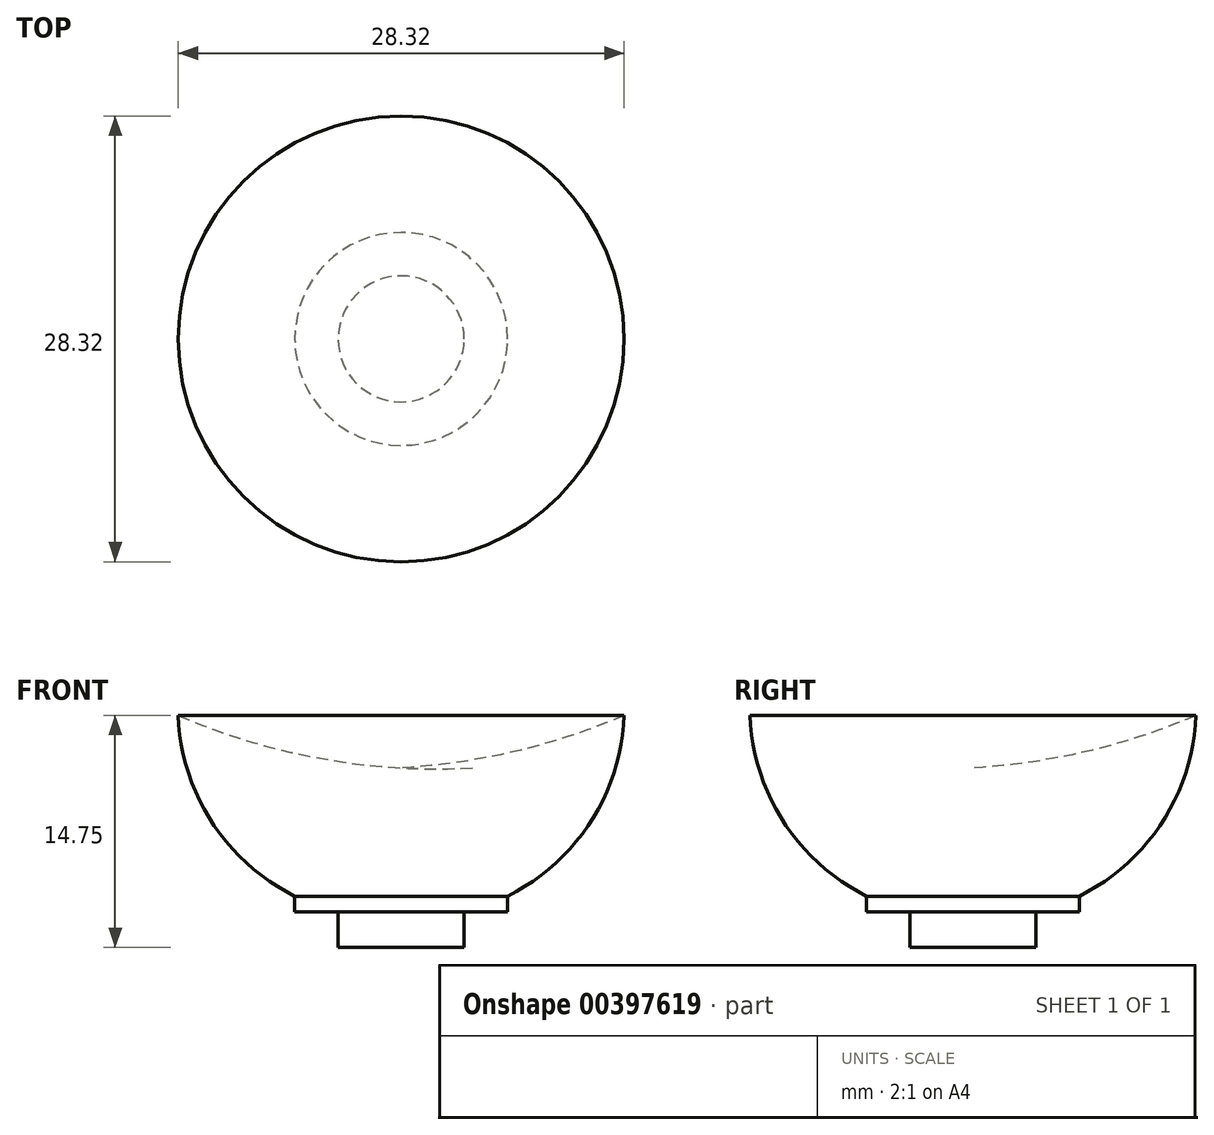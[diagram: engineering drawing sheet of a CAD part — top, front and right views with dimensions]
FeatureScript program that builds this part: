
annotation { "Feature Type Name" : "Feature", "Feature Type Description" : "" }
export const myFeature = defineFeature(function(context is Context, id is Id, definition is map)
    precondition{}
    {
        {
            var Q0;
            Q0=qCreatedBy(makeId("Front.planeOp"),FACE);
            var sketch = newSketch(context, id + "F0", { "sketchPlane" : qUnion([Q0])});
            skLineSegment(sketch, "E0", {"start": v(0, 0) * mm, "end": v(4, 0) * mm});
            skLineSegment(sketch, "E1", {"start": v(4, 0) * mm, "end": v(4, 2.25) * mm});
            skLineSegment(sketch, "E2", {"start": v(4, 2.25) * mm, "end": v(4, 14.75) * mm});
            skArc(sketch, "E3", {"start": v(4, 2.25) * mm, "mid": v(11.17, 6.8) * mm, "end": v(14.16, 14.75) * mm});
            skArc(sketch, "E4", {"start": v(0, 11.41) * mm, "mid": v(7.23, 12.46) * mm, "end": v(14.16, 14.75) * mm});
            skLineSegment(sketch, "E5", {"start": v(0, 11.41) * mm, "end": v(0, 0) * mm});
            skLineSegment(sketch, "E6", {"start": v(4, 2.25) * mm, "end": v(6.76, 2.25) * mm});
            skLineSegment(sketch, "E7", {"start": v(6.76, 2.25) * mm, "end": v(6.76, 3.26) * mm});
            skSolve(sketch);
        }
        {
            var Q0;
            Q0 = qSketchRegion(id + "F0", true);
            var Q1;
            Q1=sQuery(id+"F0.wireOp",EDGE,"E5");
            revolve(context, id + "F1", {"entities" : qUnion([Q0]), "axis" : qUnion([Q1]), "revolveType" : RevolveType.FULL});
        }
    });
